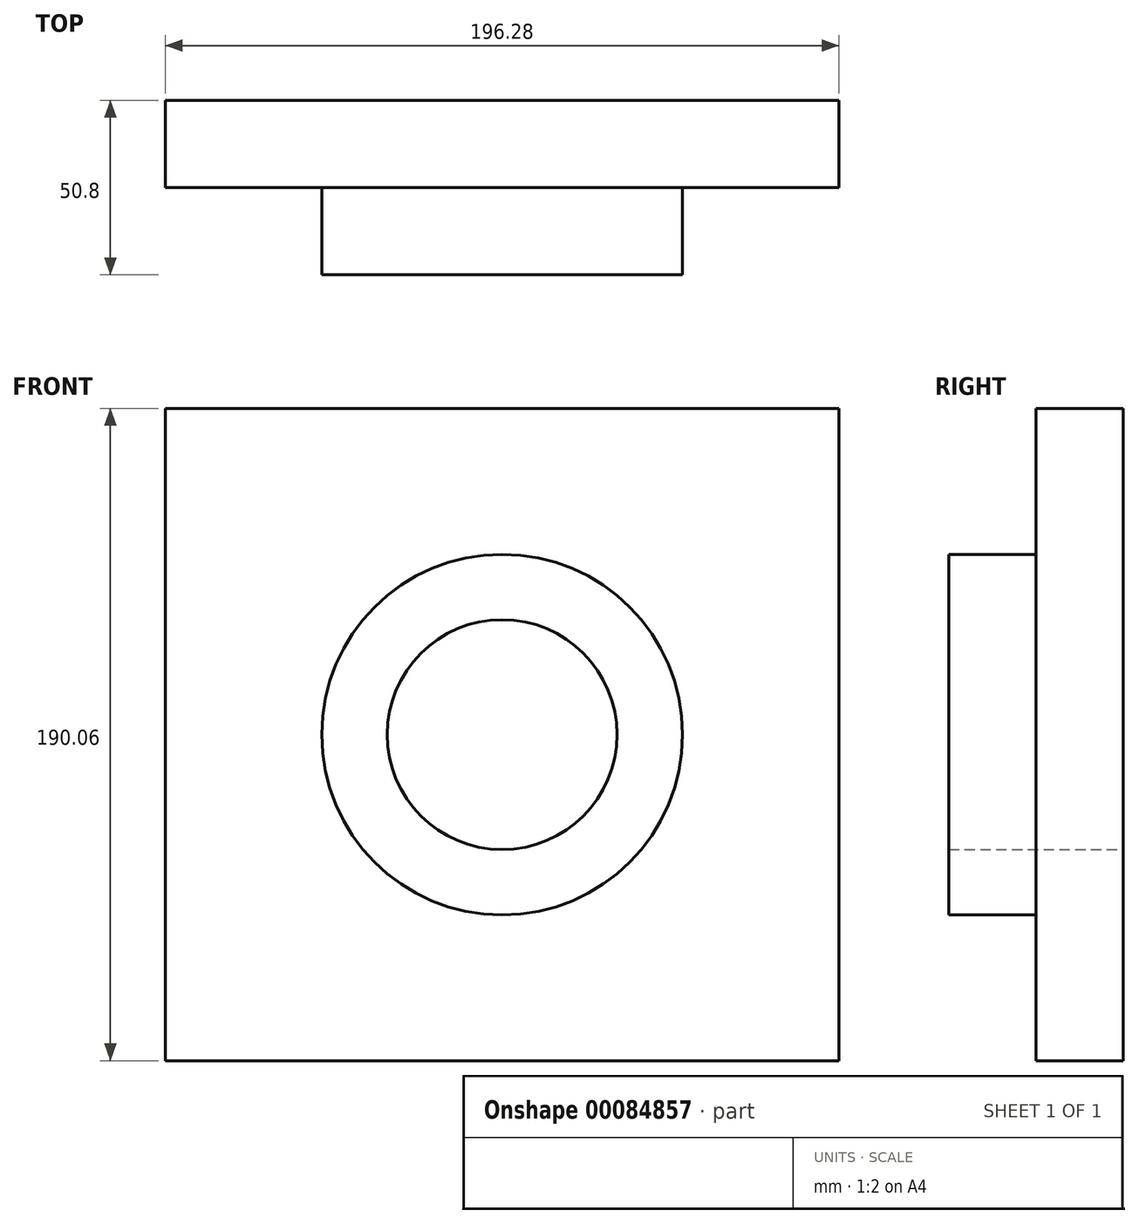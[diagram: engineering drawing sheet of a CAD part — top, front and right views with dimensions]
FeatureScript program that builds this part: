
annotation { "Feature Type Name" : "Feature", "Feature Type Description" : "" }
export const myFeature = defineFeature(function(context is Context, id is Id, definition is map)
    precondition{}
    {
        {
            var Q0;
            Q0=qCreatedBy(makeId("Front.planeOp"),FACE);
            var sketch = newSketch(context, id + "F0", { "sketchPlane" : qUnion([Q0])});
            skLineSegment(sketch, "E0.bottom", {"start": v(98.14, -95.03) * mm, "end": v(-98.14, -95.03) * mm});
            skLineSegment(sketch, "E0.top", {"start": v(98.14, 95.03) * mm, "end": v(-98.14, 95.03) * mm});
            skLineSegment(sketch, "E0.left", {"start": v(98.14, -95.03) * mm, "end": v(98.14, 95.03) * mm});
            skLineSegment(sketch, "E0.right", {"start": v(-98.14, -95.03) * mm, "end": v(-98.14, 95.03) * mm});
            skPoint(sketch, "E0.middle", {"position": v(0, 0) * mm});
            skCircle(sketch, "E1", {"center": v(0, 0) * mm, "radius": 33.5 * mm});
            skSolve(sketch);
        }
        {
            var Q0;
            Q0 = qSketchRegion(id + "F0", true);
            extrude(context, id + "F1", {"entities" : qUnion([Q0]), "depth" : 25.4 * mm});
        }
        {
            var Q0;
            Q0=makeQuery(id+"F1.opExtrude","CAP_FACE",FACE,{"disambiguationData":[OSD([sQuery(id+"F0.wireOp",EDGE,"E0.bottom"),sQuery(id+"F0.wireOp",EDGE,"E0.top"),sQuery(id+"F0.wireOp",EDGE,"E0.left"),sQuery(id+"F0.wireOp",EDGE,"E0.right"),sQuery(id+"F0.wireOp",EDGE,"E1")])],"isStart":false});
            var sketch = newSketch(context, id + "F2", { "sketchPlane" : qUnion([Q0])});
            skCircle(sketch, "E2.0", {"center": v(0, 0) * mm, "radius": 33.5 * mm});
            skCircle(sketch, "E3.0", {"center": v(0, 0) * mm, "radius": 52.55 * mm});
            skSolve(sketch);
        }
        {
            var Q0;
            Q0 = qSketchRegion(id + "F2", true);
            extrude(context, id + "F3", {"entities" : qUnion([Q0]), "operationType" : NewBodyOperationType.ADD, "depth" : 25.4 * mm});
        }
    });
